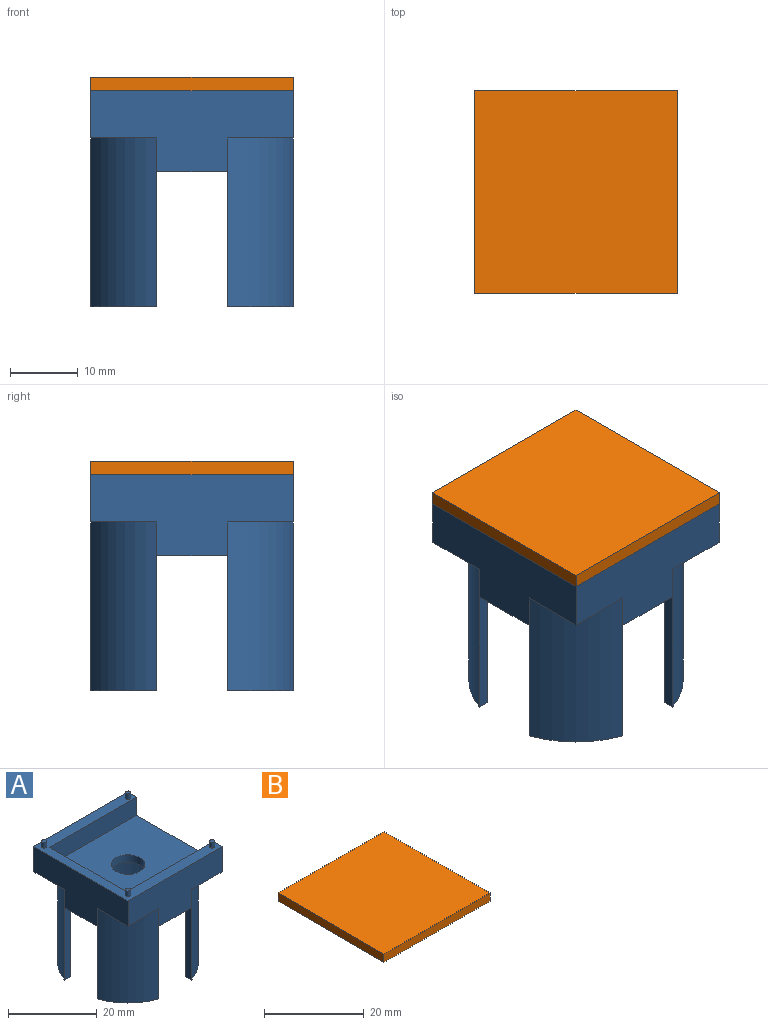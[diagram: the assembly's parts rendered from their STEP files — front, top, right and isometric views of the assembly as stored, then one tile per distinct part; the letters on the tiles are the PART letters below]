
ASSEMBLY  parts=2 mates=1
PART A: 44 faces, bbox 30x30x33.5 mm
  f0: plane 30x12mm, normal (1,0,0), area 139.5mm2, adj f1,f3,f12,f13,f15,f16,f18,f19
  f1: plane 30x12mm, normal (0,1,0), area 262mm2, adj f0,f2,f10,f15,f19,f20,f23,f32
  f2: plane 30x12mm, normal (-1,0,0), area 262mm2, adj f1,f3,f10,f11,f19,f22,f23,f29
  f3: plane 30x12mm, normal (0,-1,0), area 262mm2, adj f0,f2,f11,f12,f19,f21,f22,f26
  f4: cylinder r=14.25mm len=28.5mm, axis (0,0,1), area 1387.1mm2, adj f5,f6,f7,f8,f9,f24,f25,f26
  f5: plane 9.8x9.8mm, normal (0,0,-1), area 21.2mm2, adj f4,f20,f30,f33
  f6: plane 9.8x9.8mm, normal (0,0,-1), area 21.2mm2, adj f4,f23,f28,f31
  f7: plane 9.8x9.8mm, normal (0,0,-1), area 21.2mm2, adj f4,f22,f25,f27
  f8: plane 9.8x9.8mm, normal (0,0,-1), area 21.2mm2, adj f4,f21,f24,f34
  f9: plane 28.5x28.5mm, normal (0,0,-1), area 592.3mm2, adj f4,f14
  f10: plane 9.8x9.8mm, normal (0,0,-1), area 33.2mm2, adj f1,f2,f23
  f11: plane 9.8x9.8mm, normal (0,0,-1), area 33.2mm2, adj f2,f3,f22
  f12: plane 9.8x9.8mm, normal (0,0,-1), area 33.2mm2, adj f0,f3,f21
  f13: plane 27.75x24.5mm, normal (0,0,1), area 634.3mm2, adj f0,f14,f16,f17,f18
  f14: cylinder r=3.81mm len=7.62mm, axis (0,0,1), area 47.9mm2, adj f9,f13
  f15: plane 9.8x9.8mm, normal (0,0,-1), area 33.2mm2, adj f0,f1,f20
  f16: plane 27.75x5mm, normal (0,1,0), area 138.7mm2, adj f0,f13,f17,f19
  f17: plane 24.5x5mm, normal (1,0,0), area 122.5mm2, adj f13,f16,f18,f19
  f18: plane 27.75x5mm, normal (0,-1,0), area 138.7mm2, adj f0,f13,f17,f19
  f19: plane 30x30mm, normal (0,0,1), area 215.6mm2, adj f0,f1,f2,f3,f16,f17,f18,f36
  f20: cylinder r=15.88mm len=25mm, axis (0,0,1), area 358.6mm2, adj f0,f1,f5,f15,f30,f33
  f21: cylinder r=15.88mm len=25mm, axis (0,0,1), area 358.6mm2, adj f0,f3,f8,f12,f24,f34
  f22: cylinder r=15.88mm len=25mm, axis (0,0,1), area 358.6mm2, adj f2,f3,f7,f11,f25,f27
  f23: cylinder r=15.88mm len=25mm, axis (0,0,1), area 358.6mm2, adj f1,f2,f6,f10,f28,f31
  f24: plane 20x1.73mm, normal (-1,0,0), area 34.6mm2, adj f4,f8,f21,f26
  f25: plane 20x1.73mm, normal (1,0,0), area 34.6mm2, adj f4,f7,f22,f26
  f26: plane 10.4x1.73mm, normal (0,0,-1), area 11.1mm2, adj f3,f4,f24,f25
  f27: plane 20x1.73mm, normal (0,1,0), area 34.6mm2, adj f4,f7,f22,f29
  f28: plane 20x1.73mm, normal (0,-1,0), area 34.6mm2, adj f4,f6,f23,f29
  f29: plane 10.4x1.73mm, normal (0,0,-1), area 11.1mm2, adj f2,f4,f27,f28
  f30: plane 20x1.73mm, normal (-1,0,0), area 34.6mm2, adj f4,f5,f20,f32
  f31: plane 20x1.73mm, normal (1,0,0), area 34.6mm2, adj f4,f6,f23,f32
  f32: plane 10.4x1.73mm, normal (0,0,-1), area 11.1mm2, adj f1,f4,f30,f31
  f33: plane 20x1.73mm, normal (0,-1,0), area 34.6mm2, adj f4,f5,f20,f35
  f34: plane 20x1.73mm, normal (0,1,0), area 34.6mm2, adj f4,f8,f21,f35
  f35: plane 10.4x1.73mm, normal (0,0,-1), area 11.1mm2, adj f0,f4,f33,f34
  f36: cylinder r=0.6mm len=1.5mm, axis (0,0,-1), area 5.7mm2, adj f19,f37
  f37: plane 1.2x1.2mm, normal (0,0,1), area 1.1mm2, adj f36
  f38: cylinder r=0.6mm len=1.5mm, axis (0,0,-1), area 5.7mm2, adj f19,f39
  f39: plane 1.2x1.2mm, normal (0,0,1), area 1.1mm2, adj f38
  f40: cylinder r=0.6mm len=1.5mm, axis (0,0,-1), area 5.7mm2, adj f19,f41
  f41: plane 1.2x1.2mm, normal (0,0,1), area 1.1mm2, adj f40
  f42: cylinder r=0.6mm len=1.5mm, axis (0,0,-1), area 5.7mm2, adj f19,f43
  f43: plane 1.2x1.2mm, normal (0,0,1), area 1.1mm2, adj f42
PART B: 14 faces, bbox 30x30x2 mm
  f0: plane 30x2mm, normal (1,0,0), area 60mm2, adj f1,f3,f4,f5
  f1: plane 30x2mm, normal (0,1,0), area 60mm2, adj f0,f2,f4,f5
  f2: plane 30x2mm, normal (-1,0,0), area 60mm2, adj f1,f3,f4,f5
  f3: plane 30x2mm, normal (0,-1,0), area 60mm2, adj f0,f2,f4,f5
  f4: plane 30x30mm, normal (0,0,1), area 900mm2, adj f0,f1,f2,f3
  f5: plane 30x30mm, normal (0,0,-1), area 895.5mm2, adj f0,f1,f2,f3,f6,f8,f10,f12
  f6: cylinder r=0.6mm len=1.5mm, axis (0,0,-1), area 5.7mm2, adj f5,f7
  f7: plane 1.2x1.2mm, normal (0,0,-1), area 1.1mm2, adj f6
  f8: cylinder r=0.6mm len=1.5mm, axis (0,0,-1), area 5.7mm2, adj f5,f9
  f9: plane 1.2x1.2mm, normal (0,0,-1), area 1.1mm2, adj f8
  f10: cylinder r=0.6mm len=1.5mm, axis (0,0,-1), area 5.7mm2, adj f5,f11
  f11: plane 1.2x1.2mm, normal (0,0,-1), area 1.1mm2, adj f10
  f12: cylinder r=0.6mm len=1.5mm, axis (0,0,-1), area 5.7mm2, adj f5,f13
  f13: plane 1.2x1.2mm, normal (0,0,-1), area 1.1mm2, adj f12
PLACE A t=(0,0,6.41)mm
PLACE B t=(0,0,-9.79)mm
MATE fastened B.f6 <-> A.f40  axis (0,0,-1) through (-13.4,-13.4,11.41)mm
